# Revit family: Maxlogic Адресные модули входавыхода с сухими контактами
name_source: partatom
category: Fire Alarm Devices
units: mm (PartAtom-declared; Revit-internal decimal feet)

## family parameters
Cut with Voids When Loaded = No
Host = Face
Maintain Annotation Orientation = Yes
OmniClass Number = 23.85.30.21
OmniClass Title = Environmental Detection/Registration
Part Type = Normal
Room Calculation Point = No
Round Connector Dimension = Use Diameter
Shared = No

## types (9) — shared parameters
Manufacturer = Mavili Elektronik Ticaret A.Ş.
Model = MaxLogic
URL = https://www.mavili.com.tr
Адрес №1 = Şerifali Mahallesi Kutup Sokak No:27/1-2-4 Ümraniye TR-34775 İSTANBUL
Вес = 135 гр
Вторичный материал = Пластмассовый
Гарантийный срок = Года
Гарантийный срок запчастей = 2
Гарантия срока службы = 2
Главный Материал = Белый пластмассовый PC/ABS
Инструкция по установке = https://mavilielektronik.com
Монтажная поверхность = Настенная
Настройка адреса устройства = Модульная адресация
Номер телефона = (+)90 216 466 45 05
Номер факса = (+)90 216 466 45 10
Номинальная высота = 100 мм
Номинальная глубина = 52 мм
Номинальная ширина = 100 мм
Рабочая Температура = (-10°C) - (+55°C)
Рабочее напряжение (по умолчанию) = 26 В Пост. ток
Цвет = Белый
zero-valued in all types: Cost, Default Elevation

## per-type parameters (varying)
| type | Description | Диапазон рабочего напряжения | Код продукта | Номер позы общественных работ | Производительность кода |
| Maxlogic Адресный модуль управления релейный, 1 выход | Адресный модуль управления релейный, 1 выход | 18-33В Пост. ток | ML-1361 | 833-570 | EN 54-18 |
| Maxlogic Адресный модуль управления релейный, 1 выход, с изолятором КЗ | Адресный модуль управления релейный, 1 выход, с изолятором КЗ | 18-33В Пост. ток | ML-1361.SCI | 833-571 | EN 54-18 |
| Maxlogic Адресный модуль мониторинга контакта, 1 вход | Адресный модуль мониторинга контакта, 1 вход | 18-33В Пост. ток | ML-1362 | 833-575 | EN 54-18 |
| Maxlogic Адресный модуль мониторинга контакта, 1 вход, с изолятором КЗ | Адресный модуль мониторинга контакта, 1 вход, с изолятором КЗ | 18-33В Пост. ток | ML-1362.SCI | 833-576 | EN 54-18 |
| Maxlogic Адресный модуль I/O 2/1 (2 входа мон. Контакта / 1 выход упр. релейный) | Адресный модуль I/O 2/1 (2 входа мон. Контакта / 1 выход упр. релейный) | 18-33 В Пост. ток | ML-1363 |  | EN 54-18 |
| Maxlogic Адресный модуль I/O 2/1 (2 входа мон. Контакта / 1 выход упр. релейный), с изолятором КЗ | Адресный модуль I/O 2/1 (2 входа мон. Контакта / 1 выход упр. релейный), с изолятором КЗ | 18-33В Пост. ток | ML-1363.SCI |  | EN 54-18 |
| Maxlogic Адресный модуль I/O 4/2 (4 входа мон. Контакта / 2 выхода упр. релейных) | Адресный модуль I/O 4/2 (4 входа мон. Контакта / 2 выхода упр. релейных) | 18-33 В Пост. ток | ML-1366 |  | EN 54-18 |
| Maxlogic Адресный модуль I/O 4/2 (4 входа мон. Контакта / 2 выхода упр. релейных), с изолятором КЗ | Адресный модуль I/O 4/2 (4 входа мон. Контакта / 2 выхода упр. релейных), с изолятором КЗ | 18-33В Пост. ток | ML-1366.SCI |  | EN 54-18 |
| Maxlogic Модуль-изолятор короткого замыкания для адресной системы | Модуль-изолятор короткого замыкания для адресной системы | 18-33В Пост. ток | ML-1380 | 833-580 | EN 54-17
EN
54-17 |

## geometry (parser evidence)
native form markers: Sweep x1
no freeform markers — native parametric forms only
